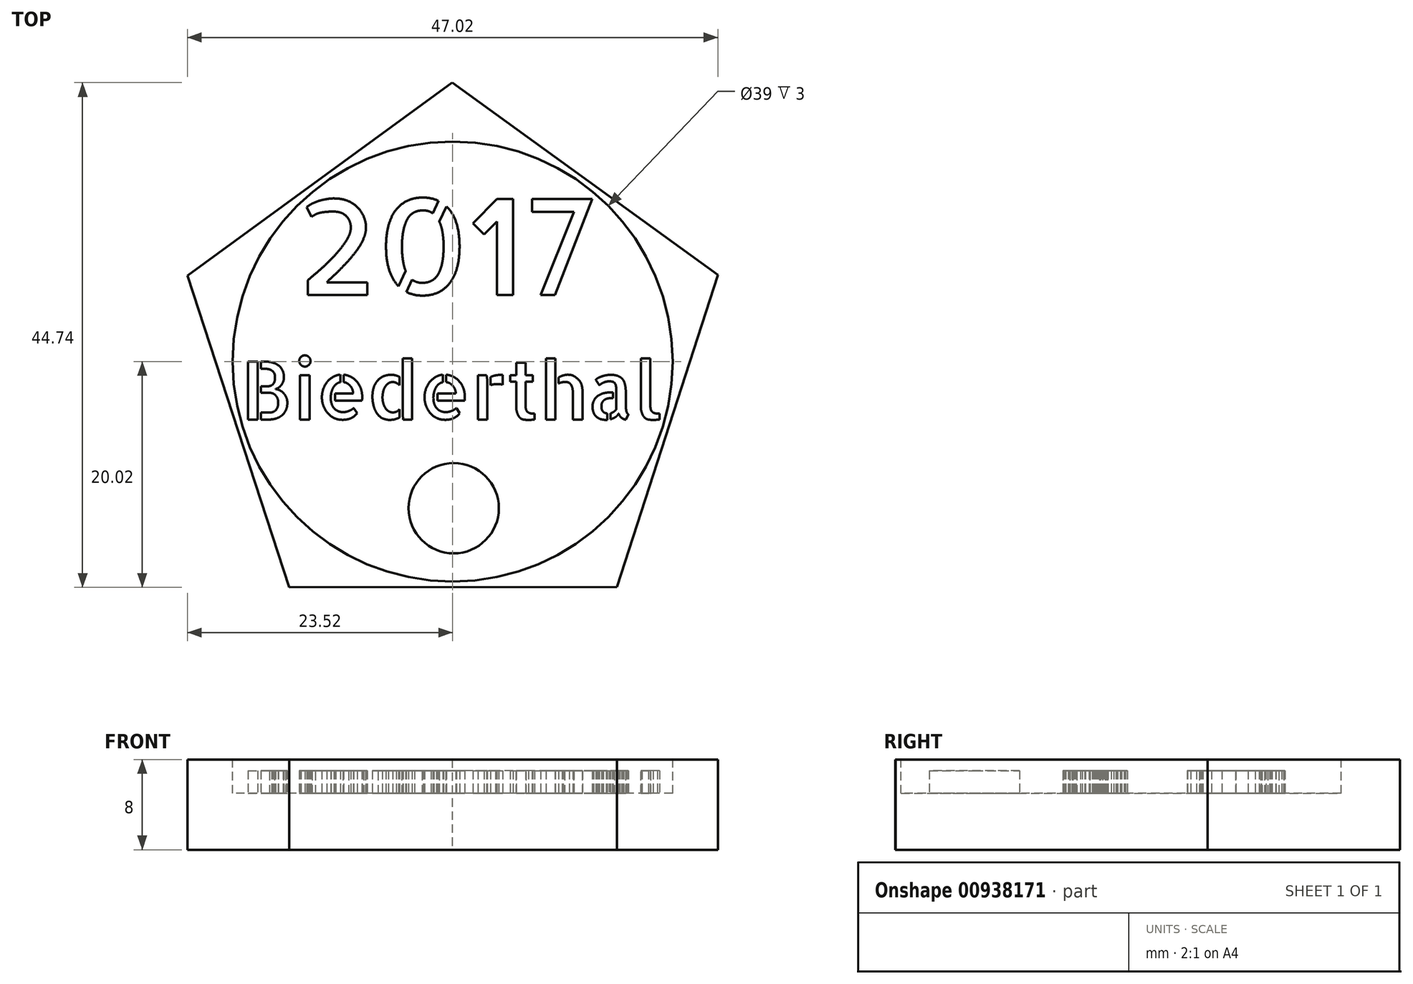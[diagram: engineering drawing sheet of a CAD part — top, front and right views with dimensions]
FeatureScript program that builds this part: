
annotation { "Feature Type Name" : "Feature", "Feature Type Description" : "" }
export const myFeature = defineFeature(function(context is Context, id is Id, definition is map)
    precondition{}
    {
        {
            var Q0;
            Q0=qCreatedBy(makeId("Top.planeOp"),FACE);
            var sketch = newSketch(context, id + "F0", { "sketchPlane" : qUnion([Q0])});
            skCircle(sketch, "E0.cCircle", {"center": v(0, 0) * mm, "radius": 20 * mm, "construction": true});
            skLineSegment(sketch, "E0.0", {"start": v(-23.52, 7.6) * mm, "end": v(-0.04, 24.72) * mm});
            skLineSegment(sketch, "E0.1", {"start": v(-0.04, 24.72) * mm, "end": v(23.5, 7.68) * mm});
            skLineSegment(sketch, "E0.2", {"start": v(23.5, 7.68) * mm, "end": v(14.56, -19.98) * mm});
            skLineSegment(sketch, "E0.3", {"start": v(14.56, -19.98) * mm, "end": v(-14.5, -20.02) * mm});
            skLineSegment(sketch, "E0.4", {"start": v(-14.5, -20.02) * mm, "end": v(-23.52, 7.6) * mm});
            skPoint(sketch, "E0.0.midPoint", {"position": v(-11.78, 16.16) * mm});
            skSolve(sketch);
        }
        {
            var Q0;
            Q0=qSketchRegion(id+"F0",true);
            extrude(context, id + "F1", {"entities" : qUnion([Q0]), "depth" : 8 * mm, "offsetDistance" : 25 * mm});
        }
        {
            var Q0;
            Q0=makeQuery(id+"F1.opExtrude","CAP_FACE",FACE,{"disambiguationData":[OSD([sQuery(id+"F0.wireOp",EDGE,"E0.0"),sQuery(id+"F0.wireOp",EDGE,"E0.1"),sQuery(id+"F0.wireOp",EDGE,"E0.2"),sQuery(id+"F0.wireOp",EDGE,"E0.3"),sQuery(id+"F0.wireOp",EDGE,"E0.4")])],"isStart":false});
            var sketch = newSketch(context, id + "F2", { "sketchPlane" : qUnion([Q0])});
            skCircle(sketch, "E1", {"center": v(0, 0) * mm, "radius": 19.5 * mm});
            skSolve(sketch);
        }
        {
            var Q0;
            {var subQ0=sQuery(id+"F2.wireOp",EDGE,"E1");var subQ4=makeQuery(id+"F2.imprint","INTERSECT",VERTEX,{"derivedFrom":[makeQuery(id+"F1.opExtrude","CAP_EDGE",EDGE,{"disambiguationData":[OSD([sQuery(id+"F0.wireOp",EDGE,"E0.0")])],"isStart":false}),subQ0]});Q0=makeQuery(id+"F2.imprint","IMPRINT",FACE,{"disambiguationData":[TD([[makeQuery(id+"F2.imprint","IMPRINT",EDGE,{"disambiguationData":[TD([[subQ4,1.0]])],"derivedFrom":subQ0}),1.0]])]});}
            extrude(context, id + "F3", {"entities" : qUnion([Q0]), "operationType" : NewBodyOperationType.REMOVE, "oppositeDirection" : true, "depth" : 3 * mm, "offsetDistance" : 25 * mm});
        }
        {
            var Q0;
            Q0=makeQuery(id+"F3.boolean.opBoolean","COPY",FACE,{"derivedFrom":makeQuery(id+"F3.opExtrude","CAP_FACE",FACE,{"disambiguationData":[OSD([sQuery(id+"F2.wireOp",EDGE,"E1")])],"isStart":false})});
            var sketch = newSketch(context, id + "F4", { "sketchPlane" : qUnion([Q0])});
            skText(sketch, "E2", { "text": "2017", "fontName": "AllertaStencil-Regular.ttf"});
            skText(sketch, "E3", { "text": "Biederthal", "fontName": "AllertaStencil-Regular.ttf"});
            skCircle(sketch, "E4", {"center": v(0.09, -13) * mm, "radius": 4 * mm});
            const initialGuessF4  = {"E2": [-0.01384, 0.0059, 1, 0, 0.0085], "E3": [-0.0188, -0.00514, 1, 0, 0.00514]};
            skSetInitialGuess(sketch, initialGuessF4);
            skSolve(sketch);
        }
        {
            var Q0;
            Q0=qSketchRegion(id+"F4",true);
            extrude(context, id + "F5", {"entities" : qUnion([Q0]), "operationType" : NewBodyOperationType.ADD, "depth" : 2 * mm, "offsetDistance" : 25 * mm});
        }
    });
